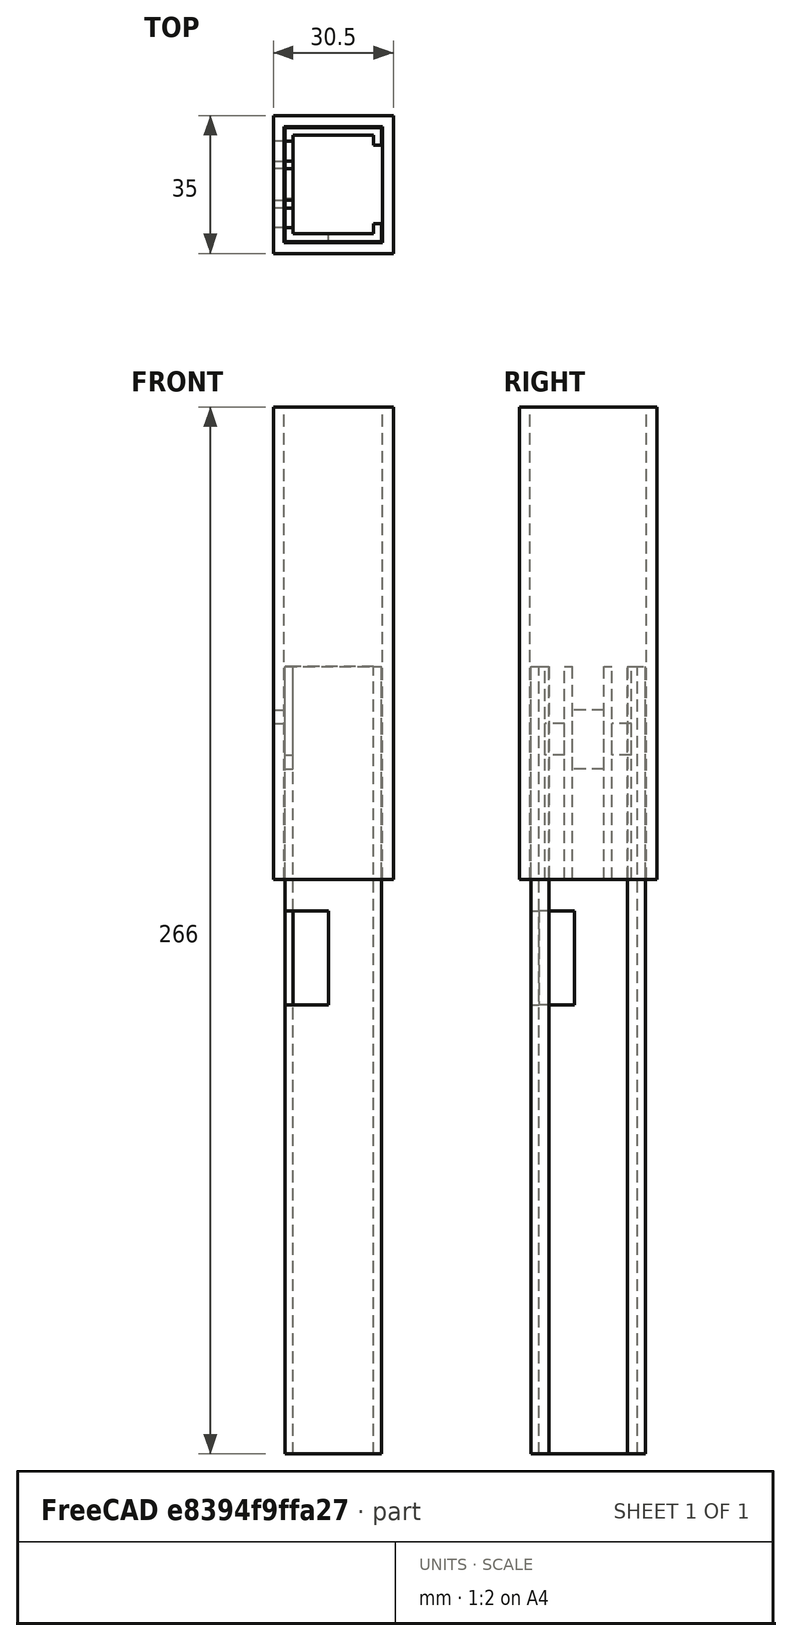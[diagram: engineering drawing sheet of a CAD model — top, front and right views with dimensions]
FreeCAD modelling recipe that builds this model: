
FCSTD DOCUMENT  (FreeCAD 0.16R6703 (Git))
Label: office-blinds
License: All rights reserved
LicenseURL: http://en.wikipedia.org/wiki/All_rights_reserved
objects: Part::Box×12, Part::Cut×5, Part::MultiFuse×3
note: 20 computed .brp shape members not serialized (recipe doc carries the construction recipe); baked Part::Feature solids carry a one-line shape summary decoded from their .brp

FEATURE [Part::Box] Box  label="Cube"
  Height = 200
  Length = 24.5
  Width = 29
FEATURE [Part::Box] Box001  label="Cube001"
  Height = 202
  Length = 20.5
  Placement = pos=(2,2,-1) rot=(0,0,1;0rad)
  Width = 25
FEATURE [Part::Box] Box002  label="Cube002"
  Height = 200
  Length = 24.5
  Placement = pos=(6,4.5,0) rot=(0,0,1;0rad)
  Width = 20
FEATURE [Part::MultiFuse] Fusion
  Shapes = -> [Box002,Box001]
FEATURE [Part::Cut] Cut
  Base = -> Box
  Tool = -> Fusion
FEATURE [Part::Box] Box003  label="Cube003"
  Height = 24
  Length = 12
  Placement = pos=(-1,-1,114) rot=(0,0,1;0rad)
  Width = 12
FEATURE [Part::Cut] Cut001
  Base = -> Cut
  Tool = -> Box003
FEATURE [Part::Box] Box004  label="Cube004"
  Height = 34
  Length = 16
  Placement = pos=(-2,10.5,174) rot=(0,0,1;0rad)
  Width = 8
FEATURE [Part::Box] Box005  label="Cube005"
  Height = 34
  Length = 16
  Placement = pos=(-2,3.5,177.5) rot=(0,0,1;0rad)
  Width = 5
FEATURE [Part::Box] Box006  label="Cube006"
  Height = 34
  Length = 16
  Placement = pos=(-2,20.5,177.5) rot=(0,0,1;0rad)
  Width = 5
FEATURE [Part::MultiFuse] Fusion001  label="slots"
  Shapes = -> [Box004,Box006,Box005]
FEATURE [Part::Cut] Cut002
  Base = -> Cut001
  Tool = -> Fusion001
FEATURE [Part::Box] Box007  label="Cube007"
  Height = 120
  Length = 30.5
  Placement = pos=(-3,-3,200) rot=(0,0,1;0rad)
  Width = 35
FEATURE [Part::Box] Box008  label="Cube008"
  Height = 200
  Length = 25
  Placement = pos=(-0.25,-0.25,190) rot=(0,0,1;0rad)
  Width = 29.5
FEATURE [Part::Cut] Cut003
  Base = -> Box007
  Placement = pos=(0,0,-54) rot=(0,0,1;0rad)
  Tool = -> Box008
FEATURE [Part::Box] Box012  label="Cube012"
  Height = 52
  Length = 16
  Placement = pos=(-5,10.5,137) rot=(0,0,1;0rad)
  Width = 8
FEATURE [Part::Box] Box013  label="Cube013"
  Height = 47
  Length = 16
  Placement = pos=(-5,20.5,138.5) rot=(0,0,1;0rad)
  Width = 5
FEATURE [Part::Box] Box014  label="Cube014"
  Height = 48
  Length = 16
  Placement = pos=(-5,3.5,137.5) rot=(0,0,1;0rad)
  Width = 5
FEATURE [Part::MultiFuse] Fusion002  label="bigslots"
  Shapes = -> [Box012,Box014,Box013]
FEATURE [Part::Cut] Cut004
  Base = -> Cut003
  Tool = -> Fusion002
